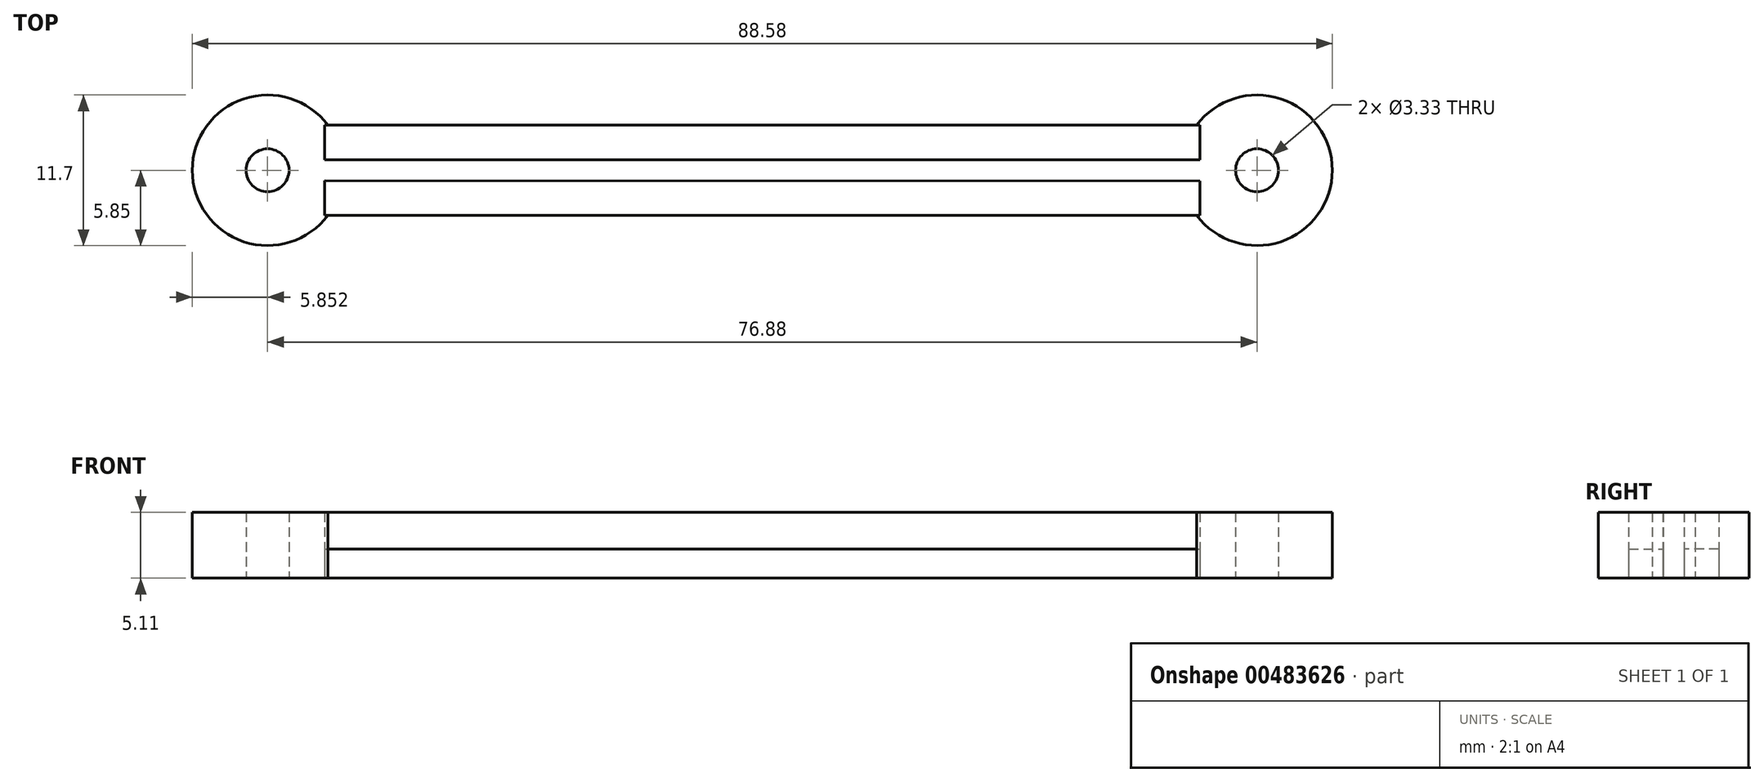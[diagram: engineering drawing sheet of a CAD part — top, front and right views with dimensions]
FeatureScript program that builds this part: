
annotation { "Feature Type Name" : "Feature", "Feature Type Description" : "" }
export const myFeature = defineFeature(function(context is Context, id is Id, definition is map)
    precondition{}
    {
        {
            var Q0;
            Q0=qCreatedBy(makeId("Top.planeOp"),FACE);
            var sketch = newSketch(context, id + "F0", { "sketchPlane" : qUnion([Q0])});
            skLineSegment(sketch, "E0.bottom", {"start": v(1.5, 0) * mm, "end": v(69.5, 0) * mm});
            skLineSegment(sketch, "E0.top", {"start": v(1.5, -7) * mm, "end": v(69.5, -7) * mm});
            skArc(sketch, "E1", {"start": v(1.74, 0) * mm, "mid": v(-8.8, -3.5) * mm, "end": v(1.74, -7) * mm});
            skPoint(sketch, "E2.start.orphan", {"position": v(1.5, -3.5) * mm});
            skLineSegment(sketch, "E3", {"start": v(1.5, 0) * mm, "end": v(1.5, -2.7) * mm});
            skLineSegment(sketch, "E4", {"start": v(1.5, -7) * mm, "end": v(1.5, -4.3) * mm});
            skArc(sketch, "E5", {"start": v(69.24, -7) * mm, "mid": v(79.78, -3.5) * mm, "end": v(69.24, 0) * mm});
            skPoint(sketch, "E0.right.start.orphan", {"position": v(69.5, -3.5) * mm});
            skLineSegment(sketch, "E6", {"start": v(69.5, -7) * mm, "end": v(69.5, -4.34) * mm});
            skLineSegment(sketch, "E7", {"start": v(69.5, 0) * mm, "end": v(69.5, -2.7) * mm});
            skCircle(sketch, "E8", {"center": v(73.93, -3.5) * mm, "radius": 1.67 * mm});
            skCircle(sketch, "E9", {"center": v(-2.95, -3.5) * mm, "radius": 1.67 * mm});
            skLineSegment(sketch, "E10", {"start": v(1.5, -2.7) * mm, "end": v(69.5, -2.7) * mm});
            skLineSegment(sketch, "E11", {"start": v(69.5, -2.7) * mm, "end": v(69.5, -4.34) * mm});
            skLineSegment(sketch, "E12", {"start": v(69.5, -4.34) * mm, "end": v(1.5, -4.3) * mm});
            skLineSegment(sketch, "E13", {"start": v(1.5, -4.3) * mm, "end": v(1.5, -2.7) * mm});
            skSolve(sketch);
        }
        {
            var Q0;
            {var subQ0=sQuery(id+"F0.wireOp",EDGE,"E3");Q0=makeQuery(id+"F0.imprint","IMPRINT",FACE,{"disambiguationData":[TD([[makeQuery(id+"F0.imprint","IMPRINT",EDGE,{"derivedFrom":subQ0}),1.0]])]});}
            var Q1;
            {var subQ4=sQuery(id+"F0.wireOp",EDGE,"E4");Q1=makeQuery(id+"F0.imprint","IMPRINT",FACE,{"disambiguationData":[TD([[makeQuery(id+"F0.imprint","IMPRINT",EDGE,{"derivedFrom":subQ4}),-1.0]])]});}
            extrude(context, id + "F1", {"entities" : qUnion([Q0, Q1]), "depth" : 2.28 * mm});
        }
        {
            var Q0;
            {var subQ1=sQuery(id+"F0.wireOp",EDGE,"E1");Q0=makeQuery(id+"F0.imprint","IMPRINT",FACE,{"disambiguationData":[TD([[makeQuery(id+"F0.imprint","IMPRINT",EDGE,{"derivedFrom":subQ1}),1.0]])]});}
            var Q1;
            Q1=makeQuery(id+"F0.imprint","IMPRINT",FACE,{"disambiguationData":[TD([[makeQuery(id+"F0.imprint","IMPRINT",EDGE,{"derivedFrom":sQuery(id+"F0.wireOp",EDGE,"E10")}),-1.0]])]});
            var Q2;
            {var subQ0=sQuery(id+"F0.wireOp",EDGE,"E5");Q2=makeQuery(id+"F0.imprint","IMPRINT",FACE,{"disambiguationData":[TD([[makeQuery(id+"F0.imprint","IMPRINT",EDGE,{"derivedFrom":subQ0}),1.0]])]});}
            extrude(context, id + "F2", {"entities" : qUnion([Q0, Q1, Q2]), "depth" : 5.11 * mm});
        }
    });
